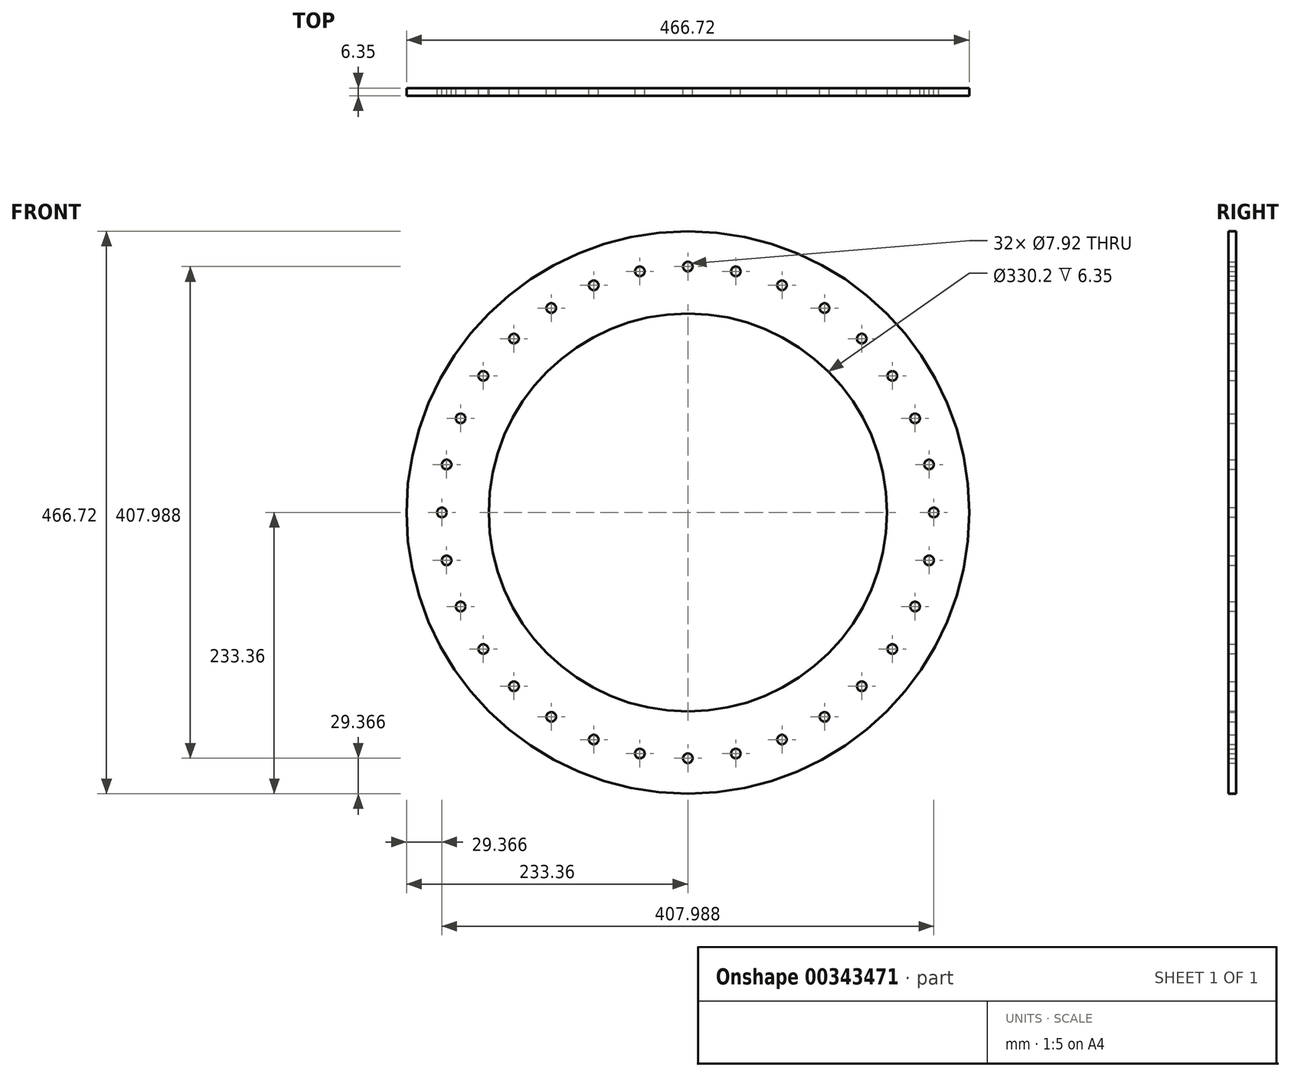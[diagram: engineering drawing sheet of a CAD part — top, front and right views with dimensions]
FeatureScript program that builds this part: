
annotation { "Feature Type Name" : "Feature", "Feature Type Description" : "" }
export const myFeature = defineFeature(function(context is Context, id is Id, definition is map)
    precondition{}
    {
        {
            var Q0;
            Q0=qCreatedBy(makeId("Front.planeOp"),FACE);
            var sketch = newSketch(context, id + "F0", { "sketchPlane" : qUnion([Q0])});
            skCircle(sketch, "E0", {"center": v(0, 0) * mm, "radius": 233.36 * mm});
            skCircle(sketch, "E1", {"center": v(0, 0) * mm, "radius": 204 * mm});
            skCircle(sketch, "E2", {"center": v(0, -204) * mm, "radius": 3.96 * mm});
            skCircle(sketch, "E3.1.0", {"center": v(39.8, -200.07) * mm, "radius": 3.96 * mm});
            skCircle(sketch, "E3.2.0", {"center": v(78.07, -188.47) * mm, "radius": 3.96 * mm});
            skCircle(sketch, "E3.3.0", {"center": v(113.33, -169.61) * mm, "radius": 3.96 * mm});
            skCircle(sketch, "E3.4.0", {"center": v(144.25, -144.25) * mm, "radius": 3.96 * mm});
            skCircle(sketch, "E3.5.0", {"center": v(169.61, -113.33) * mm, "radius": 3.96 * mm});
            skCircle(sketch, "E3.6.0", {"center": v(188.47, -78.07) * mm, "radius": 3.96 * mm});
            skCircle(sketch, "E3.7.0", {"center": v(200.07, -39.8) * mm, "radius": 3.96 * mm});
            skCircle(sketch, "E3.8.0", {"center": v(204, 0) * mm, "radius": 3.96 * mm});
            skCircle(sketch, "E3.9.0", {"center": v(200.07, 39.8) * mm, "radius": 3.96 * mm});
            skCircle(sketch, "E3.10.0", {"center": v(188.47, 78.07) * mm, "radius": 3.96 * mm});
            skCircle(sketch, "E3.11.0", {"center": v(169.61, 113.33) * mm, "radius": 3.96 * mm});
            skCircle(sketch, "E3.12.0", {"center": v(144.25, 144.25) * mm, "radius": 3.96 * mm});
            skCircle(sketch, "E3.13.0", {"center": v(113.33, 169.61) * mm, "radius": 3.96 * mm});
            skCircle(sketch, "E3.14.0", {"center": v(78.07, 188.47) * mm, "radius": 3.96 * mm});
            skCircle(sketch, "E3.15.0", {"center": v(39.8, 200.07) * mm, "radius": 3.96 * mm});
            skCircle(sketch, "E3.16.0", {"center": v(0, 204) * mm, "radius": 3.96 * mm});
            skCircle(sketch, "E3.17.0", {"center": v(-39.8, 200.07) * mm, "radius": 3.96 * mm});
            skCircle(sketch, "E3.18.0", {"center": v(-78.07, 188.47) * mm, "radius": 3.96 * mm});
            skCircle(sketch, "E3.19.0", {"center": v(-113.33, 169.61) * mm, "radius": 3.96 * mm});
            skCircle(sketch, "E3.20.0", {"center": v(-144.25, 144.25) * mm, "radius": 3.96 * mm});
            skCircle(sketch, "E3.21.0", {"center": v(-169.61, 113.33) * mm, "radius": 3.96 * mm});
            skCircle(sketch, "E3.22.0", {"center": v(-188.47, 78.07) * mm, "radius": 3.96 * mm});
            skCircle(sketch, "E3.23.0", {"center": v(-200.07, 39.8) * mm, "radius": 3.96 * mm});
            skCircle(sketch, "E3.24.0", {"center": v(-204, 0) * mm, "radius": 3.96 * mm});
            skCircle(sketch, "E3.25.0", {"center": v(-200.07, -39.8) * mm, "radius": 3.96 * mm});
            skCircle(sketch, "E3.26.0", {"center": v(-188.47, -78.07) * mm, "radius": 3.96 * mm});
            skCircle(sketch, "E3.27.0", {"center": v(-169.61, -113.33) * mm, "radius": 3.96 * mm});
            skCircle(sketch, "E3.28.0", {"center": v(-144.25, -144.25) * mm, "radius": 3.96 * mm});
            skCircle(sketch, "E3.29.0", {"center": v(-113.33, -169.61) * mm, "radius": 3.96 * mm});
            skCircle(sketch, "E3.30.0", {"center": v(-78.07, -188.47) * mm, "radius": 3.96 * mm});
            skCircle(sketch, "E3.31.0", {"center": v(-39.8, -200.07) * mm, "radius": 3.96 * mm});
            skSolve(sketch);
        }
        {
            var Q0;
            Q0 = qSketchRegion(id + "F0", true);
            var Q1;
            {var subQ1=sQuery(id+"F0.wireOp",EDGE,"E1");var subQ13=sQuery(id+"F0.wireOp",EDGE,"E3.9.0");var subQ14=makeQuery(id+"F0.imprint","INTERSECT",VERTEX,{"disambiguationData":[OD(0.0)],"derivedFrom":[subQ1,subQ13]});Q1=makeQuery(id+"F0.imprint","IMPRINT",FACE,{"disambiguationData":[TD([[makeQuery(id+"F0.imprint","IMPRINT",EDGE,{"disambiguationData":[TD([[subQ14,1.0]])],"derivedFrom":subQ1}),1.0]])]});}
            extrude(context, id + "F1", {"entities" : qUnion([Q0, Q1]), "depth" : 6.35 * mm});
        }
        {
            var Q0;
            Q0=makeQuery(id+"F1.opExtrude","CAP_FACE",FACE,{"disambiguationData":[OSD([sQuery(id+"F0.wireOp",EDGE,"E0"),sQuery(id+"F0.wireOp",EDGE,"E2"),sQuery(id+"F0.wireOp",EDGE,"E3.1.0"),sQuery(id+"F0.wireOp",EDGE,"E3.2.0"),sQuery(id+"F0.wireOp",EDGE,"E3.3.0"),sQuery(id+"F0.wireOp",EDGE,"E3.4.0"),sQuery(id+"F0.wireOp",EDGE,"E3.5.0"),sQuery(id+"F0.wireOp",EDGE,"E3.6.0"),sQuery(id+"F0.wireOp",EDGE,"E3.7.0"),sQuery(id+"F0.wireOp",EDGE,"E3.8.0"),sQuery(id+"F0.wireOp",EDGE,"E3.9.0"),sQuery(id+"F0.wireOp",EDGE,"E3.10.0"),sQuery(id+"F0.wireOp",EDGE,"E3.11.0"),sQuery(id+"F0.wireOp",EDGE,"E3.12.0"),sQuery(id+"F0.wireOp",EDGE,"E3.13.0"),sQuery(id+"F0.wireOp",EDGE,"E3.14.0"),sQuery(id+"F0.wireOp",EDGE,"E3.15.0"),sQuery(id+"F0.wireOp",EDGE,"E3.16.0"),sQuery(id+"F0.wireOp",EDGE,"E3.17.0"),sQuery(id+"F0.wireOp",EDGE,"E3.18.0"),sQuery(id+"F0.wireOp",EDGE,"E3.19.0"),sQuery(id+"F0.wireOp",EDGE,"E3.20.0"),sQuery(id+"F0.wireOp",EDGE,"E3.21.0"),sQuery(id+"F0.wireOp",EDGE,"E3.22.0"),sQuery(id+"F0.wireOp",EDGE,"E3.23.0"),sQuery(id+"F0.wireOp",EDGE,"E3.24.0"),sQuery(id+"F0.wireOp",EDGE,"E3.25.0"),sQuery(id+"F0.wireOp",EDGE,"E3.26.0"),sQuery(id+"F0.wireOp",EDGE,"E3.27.0"),sQuery(id+"F0.wireOp",EDGE,"E3.28.0"),sQuery(id+"F0.wireOp",EDGE,"E3.29.0"),sQuery(id+"F0.wireOp",EDGE,"E3.30.0"),sQuery(id+"F0.wireOp",EDGE,"E3.31.0")])],"isStart":false});
            var sketch = newSketch(context, id + "F2", { "sketchPlane" : qUnion([Q0])});
            skCircle(sketch, "E4", {"center": v(0, 0) * mm, "radius": 165.1 * mm});
            skSolve(sketch);
        }
        {
            var Q0;
            Q0 = qSketchRegion(id + "F2", true);
            extrude(context, id + "F3", {"entities" : qUnion([Q0]), "operationType" : NewBodyOperationType.REMOVE, "oppositeDirection" : true, "depth" : 6.35 * mm});
        }
    });
